# Revit family: HERZ Ball valve with T-handle and thermometer (blue) 2201
name_source: partatom
category: Rohrzubehör
units: mm (PartAtom-declared; Revit-internal decimal feet)

## family parameters
Arbeitsebenenbasiert = Nein
Beim Laden mit Abzugskörper schneiden = Nein
Bemaßung runder Anschluss = Durchmesser verwenden
Gemeinsam genutzt = Nein
Immer vertikal = Ja
OmniClass-Nummer = 23.65.55.14
OmniClass-Titel = Valves for Liquid Services
Teiletyp = Unterbricht

## types (2) — shared parameters
Application = HERZ ball valve MODUL is designed for building services such as heating and chilled water plants.
The operating conditions (temperature, pressure) should be constant.
Ball = forged brass according to EN 12165, hollow, full bore, hard chrome plated, CW617N
Ball seals = PTFE
Body = forged brass according to EN 12165, nickel plated, CW617N
Field of application = HERZ ball valves have to be used as shut off elements.
Field of application are building services, such as heating or chilled water plants.
Ball valves are used wherever the medium flow has to be reliably closed.
Ball valve should not be used as regulating element so it has to be fully opened or fully closed (the handle should not be in intermediate position).
Handle = T-handle with thermometer, blue, synthetic material PA66 GF30
Hersteller = HERZ Armaturen Ges.m.b.H
Internal threaded connectors = according to ISO 228-1
Max. operating pressure = 2500000.0 Pa
Max. operating pressure (screw connection) = 1600000.0 Pa
Max. operating temperature = 150 °C
Max. operating temperature (water - no steam) = 110 °C
Medium = Heating water quality according to ÖNORM H5195 or VDI-Standard 2035.
The use of ethylene or propylene glycol in a mixing ratio 25- 50% is allowed.
Min. operating temperature = -30 °C
Min. operating temperature (water) = 1 °C
SCRNCODE = 05;10;02
SCRNSEQ = ARM;ARM_TYP="ABVS";2
Spindle = machined brass according to EN 12164, CW614N
Spindle seals = PTFE
URL = www.herzvalves.com
W01 = 135.00°
zero-valued in all types: Vorgabe-Ansicht

## per-type parameters (varying)
| type | Dämmung |
| with insulation | Ja |
| without insulation | Nein |
